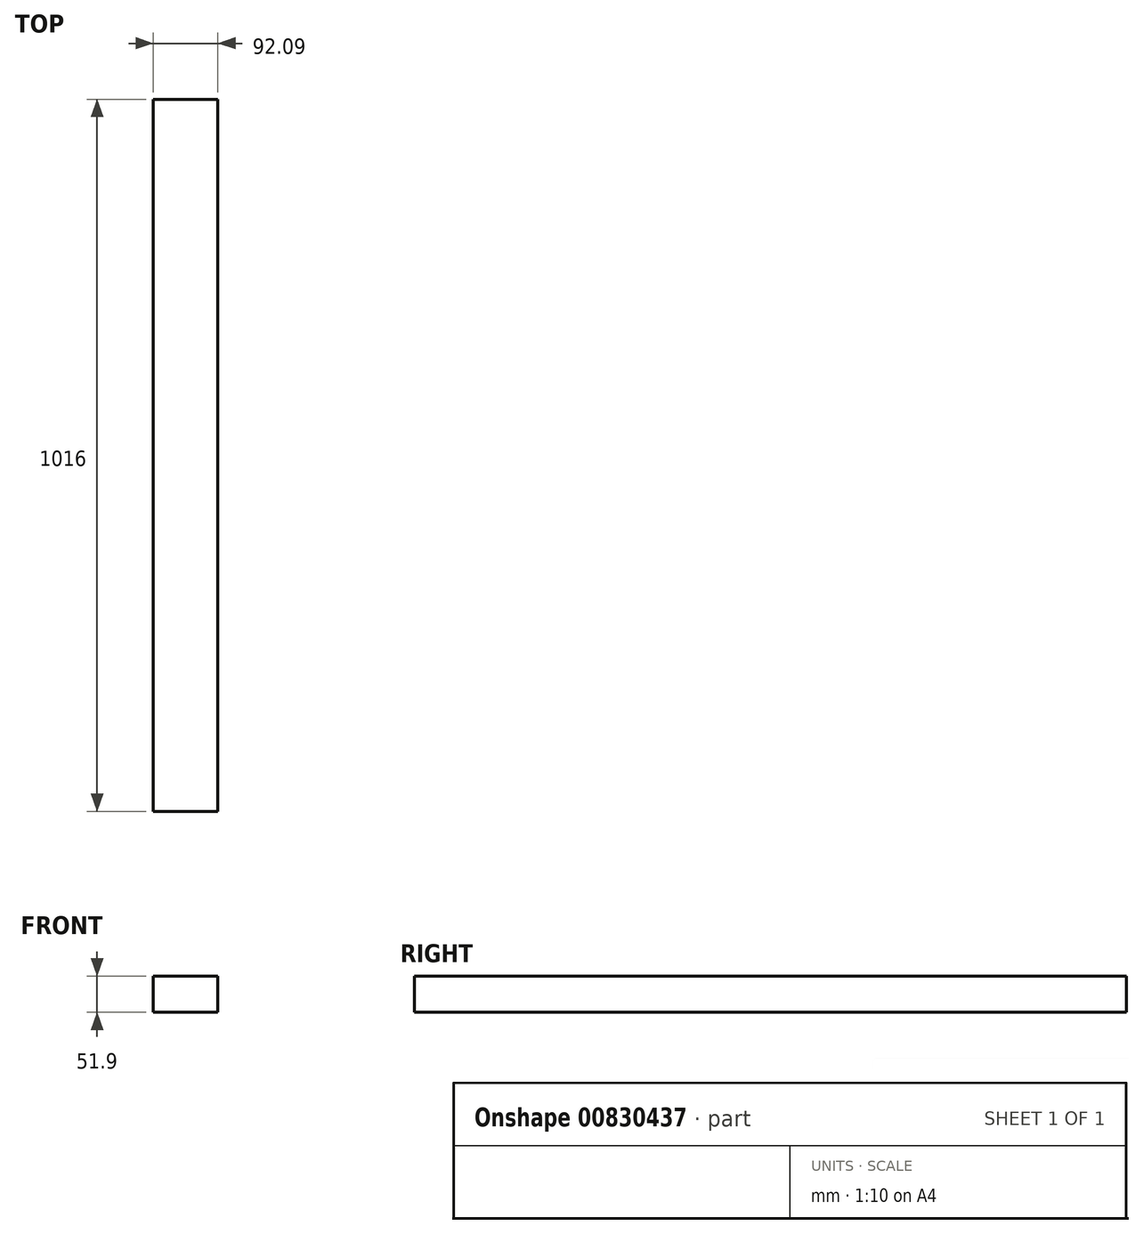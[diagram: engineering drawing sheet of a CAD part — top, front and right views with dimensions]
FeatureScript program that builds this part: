
annotation { "Feature Type Name" : "Feature", "Feature Type Description" : "" }
export const myFeature = defineFeature(function(context is Context, id is Id, definition is map)
    precondition{}
    {
        {
            var Q0;
            Q0=qCreatedBy(makeId("Front.planeOp"),FACE);
            var sketch = newSketch(context, id + "F0", { "sketchPlane" : qUnion([Q0])});
            skLineSegment(sketch, "E0.bottom", {"start": v(0, 0) * mm, "end": v(92.09, 0) * mm});
            skLineSegment(sketch, "E0.top", {"start": v(0, 51.9) * mm, "end": v(92.09, 51.9) * mm});
            skLineSegment(sketch, "E0.left", {"start": v(0, 0) * mm, "end": v(0, 51.9) * mm});
            skLineSegment(sketch, "E0.right", {"start": v(92.09, 0) * mm, "end": v(92.09, 51.9) * mm});
            skSolve(sketch);
        }
        {
            var Q0;
            Q0=makeQuery(id+"F0.imprint","IMPRINT",FACE,{"disambiguationData":[TD([[makeQuery(id+"F0.imprint","IMPRINT",EDGE,{"derivedFrom":sQuery(id+"F0.wireOp",EDGE,"E0.bottom")}),1.0]])]});
            extrude(context, id + "F1", {"entities" : qUnion([Q0]), "depth" : 1016 * mm, "offsetDistance" : 25.4 * mm});
        }
    });
